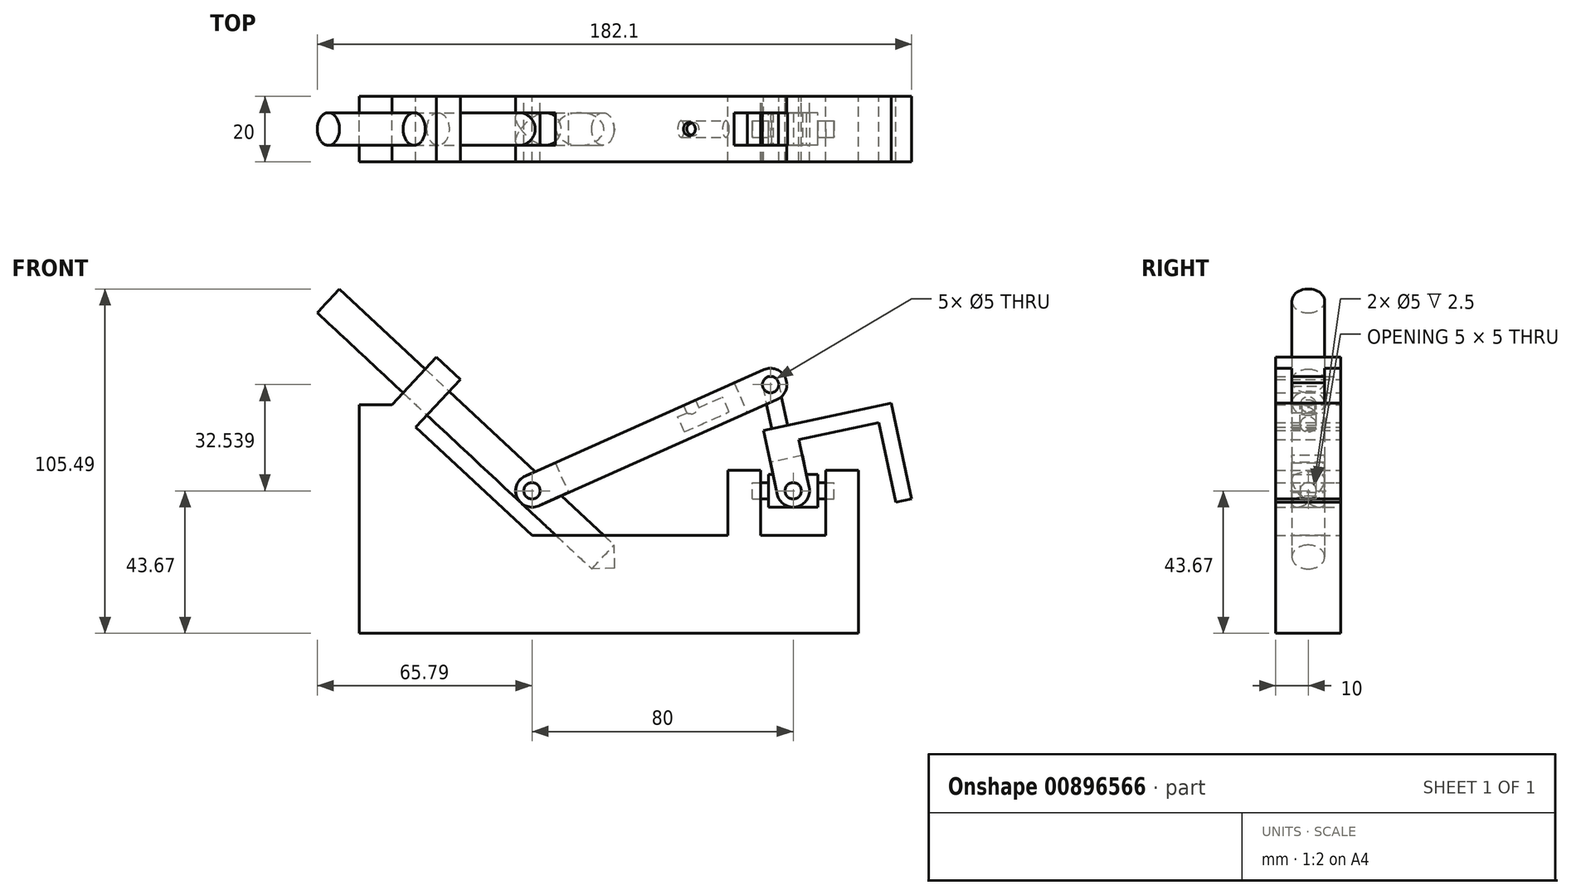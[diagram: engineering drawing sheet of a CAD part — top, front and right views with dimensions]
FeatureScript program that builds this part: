
annotation { "Feature Type Name" : "Feature", "Feature Type Description" : "" }
export const myFeature = defineFeature(function(context is Context, id is Id, definition is map)
    precondition{}
    {
        {
            var Q0;
            Q0=qCreatedBy(makeId("Front.planeOp"),FACE);
            var sketch = newSketch(context, id + "F0", { "sketchPlane" : qUnion([Q0])});
            skLineSegment(sketch, "E0", {"start": v(0, 0) * mm, "end": v(20.8, 0) * mm, "construction": true});
            skLineSegment(sketch, "E1", {"start": v(0, 0) * mm, "end": v(0, 0) * mm});
            skLineSegment(sketch, "E2", {"start": v(0, 0) * mm, "end": v(-25.24, 23.54) * mm, "construction": true});
            skLineSegment(sketch, "E3.MirrorCS", {"start": v(0, 0) * mm, "end": v(20.49, 3.61) * mm, "construction": true});
            skLineSegment(sketch, "E4", {"start": v(0, 0) * mm, "end": v(39.94, 12.21) * mm, "construction": true});
            skLineSegment(sketch, "E5.MirrorCS", {"start": v(0, 0) * mm, "end": v(19, 8.46) * mm, "construction": true});
            skLineSegment(sketch, "E6", {"start": v(19, 8.46) * mm, "end": v(20.49, 3.61) * mm, "construction": true});
            skLineSegment(sketch, "E7", {"start": v(-11.77, -12.62) * mm, "end": v(0, 0) * mm, "construction": true});
            skLineSegment(sketch, "E8", {"start": v(0, 0) * mm, "end": v(2.93, 0) * mm});
            skSolve(sketch);
        }
        {
            var Q0;
            Q0=qCreatedBy(makeId("Front.planeOp"),FACE);
            var sketch = newSketch(context, id + "F1", { "sketchPlane" : qUnion([Q0])});
            skLineSegment(sketch, "E9", {"start": v(0, 0) * mm, "end": v(0, -13.67) * mm, "construction": true});
            skLineSegment(sketch, "E10", {"start": v(0, -13.67) * mm, "end": v(-35.58, 19.5) * mm});
            skLineSegment(sketch, "E11", {"start": v(-42.9, 26.33) * mm, "end": v(-52.9, 26.33) * mm});
            skLineSegment(sketch, "E12", {"start": v(-52.9, 26.33) * mm, "end": v(-52.9, -43.67) * mm});
            skLineSegment(sketch, "E13", {"start": v(-52.9, -43.67) * mm, "end": v(70, -43.67) * mm});
            skLineSegment(sketch, "E14", {"start": v(70, -43.67) * mm, "end": v(70, -13.67) * mm, "construction": true});
            skLineSegment(sketch, "E15", {"start": v(0, -13.67) * mm, "end": v(60, -13.67) * mm});
            skLineSegment(sketch, "E16.0", {"start": v(14.66, -13.67) * mm, "end": v(-56.32, 52.52) * mm, "construction": true});
            skPoint(sketch, "E17.orphan", {"position": v(0, 0) * mm});
            skPoint(sketch, "E18.orphan", {"position": v(-25.24, 23.54) * mm});
            skLineSegment(sketch, "E19", {"start": v(-42.9, 26.33) * mm, "end": v(-29.25, 40.95) * mm});
            skLineSegment(sketch, "E20", {"start": v(-29.25, 40.95) * mm, "end": v(-21.94, 34.13) * mm});
            skLineSegment(sketch, "E21", {"start": v(-21.94, 34.13) * mm, "end": v(-35.58, 19.5) * mm});
            skLineSegment(sketch, "E22", {"start": v(70, -13.67) * mm, "end": v(70, 6.33) * mm});
            skLineSegment(sketch, "E23", {"start": v(70, 6.33) * mm, "end": v(60, 6.33) * mm});
            skLineSegment(sketch, "E24", {"start": v(60, 6.33) * mm, "end": v(60, -13.67) * mm});
            skLineSegment(sketch, "E25", {"start": v(70, -13.67) * mm, "end": v(90, -13.67) * mm});
            skLineSegment(sketch, "E26", {"start": v(90, -13.67) * mm, "end": v(90, 6.33) * mm});
            skLineSegment(sketch, "E27", {"start": v(90, 6.33) * mm, "end": v(100, 6.33) * mm});
            skLineSegment(sketch, "E28", {"start": v(100, 6.33) * mm, "end": v(100, -13.67) * mm});
            skLineSegment(sketch, "E29", {"start": v(100, -13.67) * mm, "end": v(100, -43.67) * mm});
            skLineSegment(sketch, "E30", {"start": v(70, -43.67) * mm, "end": v(100, -43.67) * mm});
            skLineSegment(sketch, "E31", {"start": v(0, -13.67) * mm, "end": v(0, -43.67) * mm, "construction": true});
            skSolve(sketch);
        }
        {
            var Q0;
            Q0=qCreatedBy(makeId("Front.planeOp"),FACE);
            var sketch = newSketch(context, id + "F2", { "sketchPlane" : qUnion([Q0])});
            skLineSegment(sketch, "E32.0", {"start": v(25.39, -23.67) * mm, "end": v(-62.38, 58.17) * mm});
            skPoint(sketch, "E33.orphan", {"position": v(-25.24, 23.54) * mm});
            skLineSegment(sketch, "E34", {"start": v(-62.38, 58.17) * mm, "end": v(-65.79, 54.5) * mm});
            skLineSegment(sketch, "E35", {"start": v(-65.79, 54.5) * mm, "end": v(18.32, -23.92) * mm});
            skPoint(sketch, "E36.orphan", {"position": v(0, 0) * mm});
            skLineSegment(sketch, "E37.0", {"start": v(0, -13.67) * mm, "end": v(60, -13.67) * mm, "construction": true});
            skLineSegment(sketch, "E38", {"start": v(25.39, -23.67) * mm, "end": v(18.32, -23.92) * mm});
            skCircle(sketch, "E39", {"center": v(0, 0) * mm, "radius": 2.5 * mm});
            skSolve(sketch);
        }
        {
            var Q0;
            Q0=qCreatedBy(makeId("Front.planeOp"),FACE);
            var sketch = newSketch(context, id + "F3", { "sketchPlane" : qUnion([Q0])});
            skCircle(sketch, "E40.0", {"center": v(0, 0) * mm, "radius": 2.5 * mm});
            skLineSegment(sketch, "E41.0", {"start": v(0, 0) * mm, "end": v(73.08, 32.54) * mm});
            skLineSegment(sketch, "E42.0", {"start": v(0, 0) * mm, "end": v(80, 0) * mm, "construction": true});
            skLineSegment(sketch, "E43.0", {"start": v(90, -13.67) * mm, "end": v(90, 6.33) * mm});
            skLineSegment(sketch, "E44.0", {"start": v(2.03, -4.57) * mm, "end": v(75.12, 27.97) * mm});
            skLineSegment(sketch, "E45.MirrorCS", {"start": v(-2.03, 4.57) * mm, "end": v(71.05, 37.1) * mm});
            skCircle(sketch, "E46", {"center": v(73.08, 32.54) * mm, "radius": 2.5 * mm});
            skArc(sketch, "E47", {"start": v(-2.03, 4.57) * mm, "mid": v(-4.57, -2.03) * mm, "end": v(2.03, -4.57) * mm});
            skArc(sketch, "E48", {"start": v(71.05, 37.1) * mm, "mid": v(77.65, 34.57) * mm, "end": v(75.12, 27.97) * mm});
            skLineSegment(sketch, "E49", {"start": v(7.1, 8.64) * mm, "end": v(11.17, -0.5) * mm});
            skPoint(sketch, "E50.orphan", {"position": v(9.14, 4.07) * mm});
            skLineSegment(sketch, "E51.0", {"start": v(11.67, 10.67) * mm, "end": v(15.74, 1.53) * mm});
            skLineSegment(sketch, "E52", {"start": v(57.35, 31) * mm, "end": v(61.41, 21.87) * mm});
            skLineSegment(sketch, "E53", {"start": v(58.77, 27.8) * mm, "end": v(47.8, 22.93) * mm});
            skLineSegment(sketch, "E54", {"start": v(45.07, 21.7) * mm, "end": v(46.29, 18.97) * mm});
            skLineSegment(sketch, "E55", {"start": v(49.03, 20.19) * mm, "end": v(60, 25.07) * mm});
            skPoint(sketch, "E56", {"position": v(45.68, 20.34) * mm});
            skLineSegment(sketch, "E57", {"start": v(45.07, 21.7) * mm, "end": v(44.66, 22.62) * mm});
            skLineSegment(sketch, "E58", {"start": v(44.66, 22.62) * mm, "end": v(47.4, 23.84) * mm});
            skLineSegment(sketch, "E59", {"start": v(47.4, 23.84) * mm, "end": v(49.43, 19.27) * mm});
            skLineSegment(sketch, "E60", {"start": v(49.43, 19.27) * mm, "end": v(46.7, 18.05) * mm});
            skLineSegment(sketch, "E61", {"start": v(46.29, 18.97) * mm, "end": v(46.7, 18.05) * mm});
            skLineSegment(sketch, "E62", {"start": v(47.4, 23.84) * mm, "end": v(58.36, 28.72) * mm});
            skLineSegment(sketch, "E63", {"start": v(49.43, 19.27) * mm, "end": v(60.4, 24.15) * mm});
            skLineSegment(sketch, "E64", {"start": v(47.4, 23.84) * mm, "end": v(46.38, 26.12) * mm});
            skLineSegment(sketch, "E65", {"start": v(48.21, 26.94) * mm, "end": v(49.63, 23.74) * mm});
            skLineSegment(sketch, "E66", {"start": v(49.43, 19.27) * mm, "end": v(50.45, 16.99) * mm});
            skLineSegment(sketch, "E67", {"start": v(61.91, 33.04) * mm, "end": v(65.98, 23.9) * mm});
            skSolve(sketch);
        }
        {
            var Q0;
            Q0=qCreatedBy(makeId("Front.planeOp"),FACE);
            var sketch = newSketch(context, id + "F4", { "sketchPlane" : qUnion([Q0])});
            skLineSegment(sketch, "E68.0", {"start": v(0, 0) * mm, "end": v(80, 0) * mm, "construction": true});
            skLineSegment(sketch, "E69.0", {"start": v(70, -13.67) * mm, "end": v(70, 6.33) * mm});
            skLineSegment(sketch, "E70.0", {"start": v(90, -13.67) * mm, "end": v(90, 6.33) * mm});
            skLineSegment(sketch, "E71", {"start": v(80, 0) * mm, "end": v(90, 0) * mm, "construction": true});
            skLineSegment(sketch, "E72.bottom", {"start": v(87.5, 5) * mm, "end": v(72.5, 5) * mm});
            skLineSegment(sketch, "E72.top", {"start": v(87.5, -5) * mm, "end": v(72.5, -5) * mm});
            skLineSegment(sketch, "E72.left", {"start": v(87.5, 5) * mm, "end": v(87.5, 2.5) * mm});
            skLineSegment(sketch, "E72.right", {"start": v(72.5, 5) * mm, "end": v(72.5, 2.5) * mm});
            skPoint(sketch, "E72.middle", {"position": v(80, 0) * mm});
            skCircle(sketch, "E73", {"center": v(80, 0) * mm, "radius": 2.5 * mm});
            skLineSegment(sketch, "E74.bottom", {"start": v(72.5, -2.5) * mm, "end": v(67.5, -2.5) * mm});
            skLineSegment(sketch, "E74.top", {"start": v(72.5, 2.5) * mm, "end": v(67.5, 2.5) * mm});
            skLineSegment(sketch, "E74.right", {"start": v(67.5, -2.5) * mm, "end": v(67.5, 2.5) * mm});
            skPoint(sketch, "E74.middle", {"position": v(70, 0) * mm});
            skLineSegment(sketch, "E75.bottom", {"start": v(87.5, -2.5) * mm, "end": v(92.5, -2.5) * mm});
            skLineSegment(sketch, "E75.top", {"start": v(87.5, 2.5) * mm, "end": v(92.5, 2.5) * mm});
            skLineSegment(sketch, "E75.right", {"start": v(92.5, -2.5) * mm, "end": v(92.5, 2.5) * mm});
            skPoint(sketch, "E75.middle", {"position": v(90, 0) * mm});
            skLineSegment(sketch, "E76.trimOffspring", {"start": v(72.5, -2.5) * mm, "end": v(72.5, -5) * mm});
            skLineSegment(sketch, "E77.trimOffspring", {"start": v(87.5, -2.5) * mm, "end": v(87.5, -5) * mm});
            skLineSegment(sketch, "E78", {"start": v(87.5, -2.5) * mm, "end": v(87.5, 2.5) * mm});
            skLineSegment(sketch, "E79", {"start": v(72.5, -2.5) * mm, "end": v(72.5, 2.5) * mm});
            skLineSegment(sketch, "E80", {"start": v(87.5, 0) * mm, "end": v(92.5, 0) * mm});
            skLineSegment(sketch, "E81", {"start": v(72.5, 0) * mm, "end": v(67.5, 0) * mm});
            skSolve(sketch);
        }
        {
            var Q0;
            Q0=qCreatedBy(makeId("Front.planeOp"),FACE);
            var sketch = newSketch(context, id + "F5", { "sketchPlane" : qUnion([Q0])});
            skCircle(sketch, "E82.0", {"center": v(80, 0) * mm, "radius": 2.5 * mm});
            skArc(sketch, "E83.0", {"start": v(70.64, 32.02) * mm, "mid": v(73.6, 30.1) * mm, "end": v(75.53, 33.06) * mm});
            skLineSegment(sketch, "E84", {"start": v(80, 0) * mm, "end": v(73.08, 32.54) * mm, "construction": true});
            skCircle(sketch, "E85.0", {"center": v(73.08, 32.54) * mm, "radius": 5 * mm, "construction": true});
            skCircle(sketch, "E86.0", {"center": v(80, 0) * mm, "radius": 5 * mm});
            skLineSegment(sketch, "E87", {"start": v(75.1, -1.04) * mm, "end": v(55.36, 91.88) * mm});
            skLineSegment(sketch, "E88.MirrorCS", {"start": v(84.9, 1.04) * mm, "end": v(81.77, 15.71) * mm});
            skPoint(sketch, "E89.orphan", {"position": v(68.2, 31.5) * mm});
            skPoint(sketch, "E90.orphan", {"position": v(77.97, 33.58) * mm});
            skArc(sketch, "E91", {"start": v(55.36, 91.88) * mm, "mid": v(59.2, 97.81) * mm, "end": v(65.14, 93.96) * mm});
            skArc(sketch, "E92", {"start": v(62.7, 93.44) * mm, "mid": v(59.73, 95.37) * mm, "end": v(57.8, 92.4) * mm});
            skLineSegment(sketch, "E93", {"start": v(57.8, 92.4) * mm, "end": v(77.55, -0.52) * mm});
            skLineSegment(sketch, "E94.MirrorCS", {"start": v(62.7, 93.44) * mm, "end": v(82.45, 0.52) * mm});
            skLineSegment(sketch, "E95", {"start": v(80.73, 20.6) * mm, "end": v(110.08, 26.84) * mm});
            skLineSegment(sketch, "E96", {"start": v(110.08, 26.84) * mm, "end": v(116.31, -2.5) * mm});
            skLineSegment(sketch, "E97.0", {"start": v(106.23, 20.9) * mm, "end": v(111.42, -3.54) * mm});
            skLineSegment(sketch, "E97.1", {"start": v(81.77, 15.71) * mm, "end": v(106.23, 20.9) * mm});
            skLineSegment(sketch, "E98", {"start": v(111.42, -3.54) * mm, "end": v(116.31, -2.5) * mm});
            skLineSegment(sketch, "E99.trimOffspring", {"start": v(80.73, 20.6) * mm, "end": v(65.14, 93.96) * mm});
            skLineSegment(sketch, "E100", {"start": v(80.73, 20.6) * mm, "end": v(70.95, 18.52) * mm});
            skLineSegment(sketch, "E101", {"start": v(82.81, 10.82) * mm, "end": v(73.03, 8.74) * mm});
            skSolve(sketch);
        }
        {
            var Q0;
            Q0=makeQuery(id+"F1.imprint","IMPRINT",FACE,{"disambiguationData":[TD([[makeQuery(id+"F1.imprint","IMPRINT",EDGE,{"derivedFrom":sQuery(id+"F1.wireOp",EDGE,"afvjlZ8D-isJQ-Fxy1-4ODG-ZcjdQYL1LsGa")}),-1.0]])]});
            var Q1;
            Q1=makeQuery(id+"F1.imprint","IMPRINT",FACE,{"disambiguationData":[TD([[makeQuery(id+"F1.imprint","IMPRINT",EDGE,{"derivedFrom":sQuery(id+"F1.wireOp",EDGE,"E10")}),1.0]])]});
            extrude(context, id + "F6", {"entities" : qUnion([Q0, Q1]), "endBound" : BoundingType.SYMMETRIC, "depth" : 20 * mm, "offsetDistance" : 25 * mm});
        }
        {
            var Q0;
            Q0=makeQuery(id+"F2.imprint","IMPRINT",FACE,{"disambiguationData":[TD([[makeQuery(id+"F2.imprint","IMPRINT",EDGE,{"derivedFrom":sQuery(id+"F2.wireOp",EDGE,"E32.0")}),1.0]])]});
            var Q1;
            {var subQ0=sQuery(id+"F2.wireOp",EDGE,"E39");var subQ1=sQuery(id+"F2.wireOp",EDGE,"E32.0");var subQ2=makeQuery(id+"F2.imprint","INTERSECT",VERTEX,{"disambiguationData":[OD(0.0)],"derivedFrom":[subQ1,subQ0]});Q1=makeQuery(id+"F2.imprint","IMPRINT",FACE,{"disambiguationData":[TD([[makeQuery(id+"F2.imprint","IMPRINT",EDGE,{"disambiguationData":[TD([[subQ2,-1.0]])],"derivedFrom":subQ1}),1.0]])]});}
            var Q2;
            Q2=sQuery(id+"F2.wireOp",EDGE,"E32.0");
            revolve(context, id + "F7", {"surfaceOperationType" : NewSurfaceOperationType.NEW, "entities" : qUnion([Q0, Q1]), "axis" : qUnion([Q2]), "revolveType" : RevolveType.FULL});
        }
        {
            var Q0;
            {var subQ0=sQuery(id+"F2.wireOp",EDGE,"E39");var subQ1=sQuery(id+"F2.wireOp",EDGE,"E32.0");var subQ2=makeQuery(id+"F2.imprint","INTERSECT",VERTEX,{"disambiguationData":[OD(0.0)],"derivedFrom":[subQ1,subQ0]});Q0=makeQuery(id+"F2.imprint","IMPRINT",FACE,{"disambiguationData":[TD([[makeQuery(id+"F2.imprint","IMPRINT",EDGE,{"disambiguationData":[TD([[subQ2,-1.0]])],"derivedFrom":subQ1}),1.0]])]});}
            var Q1;
            {var subQ0=sQuery(id+"F2.wireOp",EDGE,"E39");var subQ1=sQuery(id+"F2.wireOp",EDGE,"E32.0");var subQ2=makeQuery(id+"F2.imprint","INTERSECT",VERTEX,{"disambiguationData":[OD(0.0)],"derivedFrom":[subQ1,subQ0]});Q1=makeQuery(id+"F2.imprint","IMPRINT",FACE,{"disambiguationData":[TD([[makeQuery(id+"F2.imprint","IMPRINT",EDGE,{"disambiguationData":[TD([[subQ2,-1.0]])],"derivedFrom":subQ1}),-1.0]])]});}
            extrude(context, id + "F8", {"entities" : qUnion([Q0, Q1]), "operationType" : NewBodyOperationType.REMOVE, "endBound" : BoundingType.SYMMETRIC, "oppositeDirection" : true, "depth" : 25 * mm, "offsetDistance" : 25 * mm});
        }
        {
            var Q0;
            Q0=makeQuery(id+"F7.opRevolve","SWEPT_BODY",BODY,{"disambiguationData":[OSD([sQuery(id+"F2.wireOp",EDGE,"E32.0"),sQuery(id+"F2.wireOp",EDGE,"E34"),sQuery(id+"F2.wireOp",EDGE,"E35"),sQuery(id+"F2.wireOp",EDGE,"E38")])]});
            var Q1;
            Q1=makeQuery(id+"F6.opExtrude","SWEPT_BODY",BODY,{"disambiguationData":[OSD([sQuery(id+"F1.wireOp",EDGE,"E10"),sQuery(id+"F1.wireOp",EDGE,"E11"),sQuery(id+"F1.wireOp",EDGE,"E12"),sQuery(id+"F1.wireOp",EDGE,"E13"),sQuery(id+"F1.wireOp",EDGE,"E15"),sQuery(id+"F1.wireOp",EDGE,"E19"),sQuery(id+"F1.wireOp",EDGE,"E20"),sQuery(id+"F1.wireOp",EDGE,"E21"),sQuery(id+"F1.wireOp",EDGE,"E22"),sQuery(id+"F1.wireOp",EDGE,"E23"),sQuery(id+"F1.wireOp",EDGE,"E24"),sQuery(id+"F1.wireOp",EDGE,"E25"),sQuery(id+"F1.wireOp",EDGE,"E26"),sQuery(id+"F1.wireOp",EDGE,"E27"),sQuery(id+"F1.wireOp",EDGE,"E28"),sQuery(id+"F1.wireOp",EDGE,"E29"),sQuery(id+"F1.wireOp",EDGE,"E30")])]});
            booleanBodies(context, id + "F9", {"operationType" : BooleanOperationType.SUBTRACTION, "tools" : qUnion([Q0]), "targets" : qUnion([Q1]), "keepTools" : true});
        }
        {
            var Q0;
            Q0=makeQuery(id+"F3.imprint","IMPRINT",FACE,{"disambiguationData":[TD([[makeQuery(id+"F3.imprint","IMPRINT",EDGE,{"derivedFrom":sQuery(id+"F3.wireOp",EDGE,"E40.0")}),-1.0]])]});
            var Q1;
            {var subQ0=sQuery(id+"F3.wireOp",EDGE,"E49");var subQ1=sQuery(id+"F3.wireOp",EDGE,"E41.0");var subQ2=makeQuery(id+"F3.imprint","INTERSECT",VERTEX,{"derivedFrom":[subQ1,subQ0]});Q1=makeQuery(id+"F3.imprint","IMPRINT",FACE,{"disambiguationData":[TD([[makeQuery(id+"F3.imprint","IMPRINT",EDGE,{"disambiguationData":[TD([[subQ2,-1.0]])],"derivedFrom":subQ1}),1.0]])]});}
            var Q2;
            {var subQ0=sQuery(id+"F3.wireOp",EDGE,"E49");var subQ1=sQuery(id+"F3.wireOp",EDGE,"E41.0");var subQ2=makeQuery(id+"F3.imprint","INTERSECT",VERTEX,{"derivedFrom":[subQ1,subQ0]});Q2=makeQuery(id+"F3.imprint","IMPRINT",FACE,{"disambiguationData":[TD([[makeQuery(id+"F3.imprint","IMPRINT",EDGE,{"disambiguationData":[TD([[subQ2,-1.0]])],"derivedFrom":subQ1}),-1.0]])]});}
            var Q3;
            Q3=makeQuery(id+"F3.imprint","IMPRINT",FACE,{"disambiguationData":[TD([[makeQuery(id+"F3.imprint","IMPRINT",EDGE,{"derivedFrom":sQuery(id+"F3.wireOp",EDGE,"E46")}),-1.0]])]});
            var Q4;
            {var subQ5=sQuery(id+"F3.wireOp",EDGE,"E67");var subQ6=sQuery(id+"F3.wireOp",EDGE,"E41.0");var subQ7=makeQuery(id+"F3.imprint","INTERSECT",VERTEX,{"derivedFrom":[subQ6,subQ5]});Q4=makeQuery(id+"F3.imprint","IMPRINT",FACE,{"disambiguationData":[TD([[makeQuery(id+"F3.imprint","IMPRINT",EDGE,{"disambiguationData":[TD([[subQ7,1.0]])],"derivedFrom":subQ6}),1.0]])]});}
            var Q5;
            {var subQ2=sQuery(id+"F3.wireOp",EDGE,"E41.0");var subQ7=sQuery(id+"F3.wireOp",EDGE,"E67");var subQ9=makeQuery(id+"F3.imprint","INTERSECT",VERTEX,{"derivedFrom":[subQ2,subQ7]});Q5=makeQuery(id+"F3.imprint","IMPRINT",FACE,{"disambiguationData":[TD([[makeQuery(id+"F3.imprint","IMPRINT",EDGE,{"disambiguationData":[TD([[subQ9,1.0]])],"derivedFrom":subQ2}),-1.0]])]});}
            extrude(context, id + "F10", {"entities" : qUnion([Q0, Q1, Q2, Q3, Q4, Q5]), "endBound" : BoundingType.SYMMETRIC, "depth" : 20 * mm, "offsetDistance" : 25 * mm});
        }
        {
            var Q0;
            {var subQ4=sQuery(id+"F3.wireOp",EDGE,"E52");var subQ6=sQuery(id+"F3.wireOp",EDGE,"E41.0");var subQ7=makeQuery(id+"F3.imprint","INTERSECT",VERTEX,{"derivedFrom":[subQ6,subQ4]});Q0=makeQuery(id+"F3.imprint","IMPRINT",FACE,{"disambiguationData":[TD([[makeQuery(id+"F3.imprint","IMPRINT",EDGE,{"disambiguationData":[TD([[subQ7,1.0]])],"derivedFrom":subQ6}),1.0]])]});}
            var Q1;
            {var subQ1=sQuery(id+"F3.wireOp",EDGE,"E57");Q1=makeQuery(id+"F3.imprint","IMPRINT",FACE,{"disambiguationData":[TD([[makeQuery(id+"F3.imprint","IMPRINT",EDGE,{"derivedFrom":subQ1}),-1.0]])]});}
            var Q2;
            Q2=sQuery(id+"F3.wireOp",EDGE,"E41.0");
            revolve(context, id + "F11", {"operationType" : NewBodyOperationType.ADD, "surfaceOperationType" : NewSurfaceOperationType.NEW, "entities" : qUnion([Q0, Q1]), "axis" : qUnion([Q2]), "revolveType" : RevolveType.FULL});
        }
        {
            var Q0;
            {var subQ0=sQuery(id+"F3.wireOp",EDGE,"E57");Q0=makeQuery(id+"F3.imprint","IMPRINT",FACE,{"disambiguationData":[TD([[makeQuery(id+"F3.imprint","IMPRINT",EDGE,{"derivedFrom":subQ0}),1.0]])]});}
            var Q1;
            Q1=makeQuery(id+"F3.imprint","IMPRINT",FACE,{"disambiguationData":[TD([[makeQuery(id+"F3.imprint","IMPRINT",EDGE,{"derivedFrom":sQuery(id+"F3.wireOp",EDGE,"E60")}),1.0]])]});
            var Q2;
            {var subQ0=sQuery(id+"F3.wireOp",EDGE,"E64");Q2=makeQuery(id+"F3.imprint","IMPRINT",FACE,{"disambiguationData":[TD([[makeQuery(id+"F3.imprint","IMPRINT",EDGE,{"derivedFrom":subQ0}),-1.0]])]});}
            var Q3;
            {var subQ0=sQuery(id+"F3.wireOp",EDGE,"E59");var subQ1=sQuery(id+"F3.wireOp",EDGE,"E53");var subQ2=makeQuery(id+"F3.imprint","INTERSECT",VERTEX,{"derivedFrom":[subQ1,subQ0]});Q3=makeQuery(id+"F3.imprint","IMPRINT",FACE,{"disambiguationData":[TD([[makeQuery(id+"F3.imprint","IMPRINT",EDGE,{"disambiguationData":[TD([[subQ2,1.0]])],"derivedFrom":subQ1}),-1.0]])]});}
            var Q4;
            {var subQ0=sQuery(id+"F3.wireOp",EDGE,"E53");var subQ1=sQuery(id+"F3.wireOp",EDGE,"E52");var subQ2=makeQuery(id+"F3.imprint","INTERSECT",VERTEX,{"derivedFrom":[subQ1,subQ0]});Q4=makeQuery(id+"F3.imprint","IMPRINT",FACE,{"disambiguationData":[TD([[makeQuery(id+"F3.imprint","IMPRINT",EDGE,{"disambiguationData":[TD([[subQ2,1.0]])],"derivedFrom":subQ1}),-1.0]])]});}
            var Q5;
            {var subQ0=sQuery(id+"F3.wireOp",EDGE,"E52");var subQ1=sQuery(id+"F3.wireOp",EDGE,"E45.MirrorCS");var subQ2=makeQuery(id+"F3.imprint","INTERSECT",VERTEX,{"derivedFrom":[subQ1,subQ0]});Q5=makeQuery(id+"F3.imprint","IMPRINT",FACE,{"disambiguationData":[TD([[makeQuery(id+"F3.imprint","IMPRINT",EDGE,{"disambiguationData":[TD([[subQ2,1.0]])],"derivedFrom":subQ1}),-1.0]])]});}
            var Q6;
            {var subQ0=sQuery(id+"F3.wireOp",EDGE,"E55");Q6=makeQuery(id+"F3.imprint","IMPRINT",FACE,{"disambiguationData":[TD([[makeQuery(id+"F3.imprint","IMPRINT",EDGE,{"derivedFrom":subQ0}),-1.0]])]});}
            var Q7;
            {var subQ4=sQuery(id+"F3.wireOp",EDGE,"E63");Q7=makeQuery(id+"F3.imprint","IMPRINT",FACE,{"disambiguationData":[TD([[makeQuery(id+"F3.imprint","IMPRINT",EDGE,{"derivedFrom":subQ4}),-1.0]])]});}
            var Q8;
            {var subQ1=sQuery(id+"F3.wireOp",EDGE,"E57");Q8=makeQuery(id+"F3.imprint","IMPRINT",FACE,{"disambiguationData":[TD([[makeQuery(id+"F3.imprint","IMPRINT",EDGE,{"derivedFrom":subQ1}),-1.0]])]});}
            var Q9;
            {var subQ2=sQuery(id+"F3.wireOp",EDGE,"E60");Q9=makeQuery(id+"F3.imprint","IMPRINT",FACE,{"disambiguationData":[TD([[makeQuery(id+"F3.imprint","IMPRINT",EDGE,{"derivedFrom":subQ2}),-1.0]])]});}
            var Q10;
            {var subQ4=sQuery(id+"F3.wireOp",EDGE,"E52");var subQ6=sQuery(id+"F3.wireOp",EDGE,"E41.0");var subQ7=makeQuery(id+"F3.imprint","INTERSECT",VERTEX,{"derivedFrom":[subQ6,subQ4]});Q10=makeQuery(id+"F3.imprint","IMPRINT",FACE,{"disambiguationData":[TD([[makeQuery(id+"F3.imprint","IMPRINT",EDGE,{"disambiguationData":[TD([[subQ7,1.0]])],"derivedFrom":subQ6}),1.0]])]});}
            var Q11;
            {var subQ5=sQuery(id+"F3.wireOp",EDGE,"E55");Q11=makeQuery(id+"F3.imprint","IMPRINT",FACE,{"disambiguationData":[TD([[makeQuery(id+"F3.imprint","IMPRINT",EDGE,{"derivedFrom":subQ5}),1.0]])]});}
            extrude(context, id + "F12", {"entities" : qUnion([Q0, Q1, Q2, Q3, Q4, Q5, Q6, Q7, Q8, Q9, Q10, Q11]), "operationType" : NewBodyOperationType.ADD, "endBound" : BoundingType.SYMMETRIC, "depth" : 20 * mm, "offsetDistance" : 25 * mm});
        }
        {
            var Q0;
            {var subQ1=sQuery(id+"F3.wireOp",EDGE,"E57");Q0=makeQuery(id+"F3.imprint","IMPRINT",FACE,{"disambiguationData":[TD([[makeQuery(id+"F3.imprint","IMPRINT",EDGE,{"derivedFrom":subQ1}),-1.0]])]});}
            var Q1;
            {var subQ4=sQuery(id+"F3.wireOp",EDGE,"E52");var subQ6=sQuery(id+"F3.wireOp",EDGE,"E41.0");var subQ7=makeQuery(id+"F3.imprint","INTERSECT",VERTEX,{"derivedFrom":[subQ6,subQ4]});Q1=makeQuery(id+"F3.imprint","IMPRINT",FACE,{"disambiguationData":[TD([[makeQuery(id+"F3.imprint","IMPRINT",EDGE,{"disambiguationData":[TD([[subQ7,1.0]])],"derivedFrom":subQ6}),1.0]])]});}
            var Q2;
            {var subQ0=sQuery(id+"F3.wireOp",EDGE,"E59");var subQ1=sQuery(id+"F3.wireOp",EDGE,"E53");var subQ2=makeQuery(id+"F3.imprint","INTERSECT",VERTEX,{"derivedFrom":[subQ1,subQ0]});Q2=makeQuery(id+"F3.imprint","IMPRINT",FACE,{"disambiguationData":[TD([[makeQuery(id+"F3.imprint","IMPRINT",EDGE,{"disambiguationData":[TD([[subQ2,1.0]])],"derivedFrom":subQ1}),-1.0]])]});}
            var Q3;
            {var subQ0=sQuery(id+"F3.wireOp",EDGE,"E53");var subQ1=sQuery(id+"F3.wireOp",EDGE,"E52");var subQ2=makeQuery(id+"F3.imprint","INTERSECT",VERTEX,{"derivedFrom":[subQ1,subQ0]});Q3=makeQuery(id+"F3.imprint","IMPRINT",FACE,{"disambiguationData":[TD([[makeQuery(id+"F3.imprint","IMPRINT",EDGE,{"disambiguationData":[TD([[subQ2,1.0]])],"derivedFrom":subQ1}),-1.0]])]});}
            var Q4;
            Q4=sQuery(id+"F3.wireOp",EDGE,"E41.0");
            revolve(context, id + "F13", {"operationType" : NewBodyOperationType.REMOVE, "surfaceOperationType" : NewSurfaceOperationType.NEW, "entities" : qUnion([Q0, Q1, Q2, Q3]), "axis" : qUnion([Q4]), "revolveType" : RevolveType.FULL, "oppositeDirection" : true});
        }
        {
            var Q0;
            {var subQ0=sQuery(id+"F3.wireOp",EDGE,"E64");Q0=makeQuery(id+"F3.imprint","IMPRINT",FACE,{"disambiguationData":[TD([[makeQuery(id+"F3.imprint","IMPRINT",EDGE,{"derivedFrom":subQ0}),-1.0]])]});}
            var Q1;
            {var subQ0=sQuery(id+"F3.wireOp",EDGE,"E59");var subQ1=sQuery(id+"F3.wireOp",EDGE,"E53");var subQ2=makeQuery(id+"F3.imprint","INTERSECT",VERTEX,{"derivedFrom":[subQ1,subQ0]});Q1=makeQuery(id+"F3.imprint","IMPRINT",FACE,{"disambiguationData":[TD([[makeQuery(id+"F3.imprint","IMPRINT",EDGE,{"disambiguationData":[TD([[subQ2,1.0]])],"derivedFrom":subQ1}),-1.0]])]});}
            var Q2;
            Q2=sQuery(id+"F3.wireOp",EDGE,"E65");
            revolve(context, id + "F14", {"operationType" : NewBodyOperationType.REMOVE, "surfaceOperationType" : NewSurfaceOperationType.NEW, "entities" : qUnion([Q0, Q1]), "axis" : qUnion([Q2]), "revolveType" : RevolveType.FULL, "oppositeDirection" : true});
        }
        {
            var Q0;
            Q0=makeQuery(id+"F3.imprint","IMPRINT",FACE,{"disambiguationData":[TD([[makeQuery(id+"F3.imprint","IMPRINT",EDGE,{"derivedFrom":sQuery(id+"F3.wireOp",EDGE,"E40.0")}),-1.0]])]});
            var Q1;
            Q1=makeQuery(id+"F3.imprint","IMPRINT",FACE,{"disambiguationData":[TD([[makeQuery(id+"F3.imprint","IMPRINT",EDGE,{"derivedFrom":sQuery(id+"F3.wireOp",EDGE,"E46")}),-1.0]])]});
            extrude(context, id + "F15", {"entities" : qUnion([Q0, Q1]), "operationType" : NewBodyOperationType.REMOVE, "endBound" : BoundingType.SYMMETRIC, "depth" : 10 * mm, "offsetDistance" : 25 * mm});
        }
        {
            var Q0;
            {var subQ0=sQuery(id+"F4.wireOp",EDGE,"E74.top");var subQ1=sQuery(id+"F4.wireOp",EDGE,"E69.0");var subQ2=makeQuery(id+"F4.imprint","INTERSECT",VERTEX,{"derivedFrom":[subQ1,subQ0]});Q0=makeQuery(id+"F4.imprint","IMPRINT",FACE,{"disambiguationData":[TD([[makeQuery(id+"F4.imprint","IMPRINT",EDGE,{"disambiguationData":[TD([[subQ2,1.0]])],"derivedFrom":subQ1}),-1.0]])]});}
            var Q1;
            {var subQ0=sQuery(id+"F4.wireOp",EDGE,"E75.top");var subQ1=sQuery(id+"F4.wireOp",EDGE,"E70.0");var subQ2=makeQuery(id+"F4.imprint","INTERSECT",VERTEX,{"derivedFrom":[subQ1,subQ0]});Q1=makeQuery(id+"F4.imprint","IMPRINT",FACE,{"disambiguationData":[TD([[makeQuery(id+"F4.imprint","IMPRINT",EDGE,{"disambiguationData":[TD([[subQ2,1.0]])],"derivedFrom":subQ1}),1.0]])]});}
            var Q2;
            {var subQ0=sQuery(id+"F4.wireOp",EDGE,"E74.top");var subQ1=sQuery(id+"F4.wireOp",EDGE,"E69.0");var subQ2=makeQuery(id+"F4.imprint","INTERSECT",VERTEX,{"derivedFrom":[subQ1,subQ0]});Q2=makeQuery(id+"F4.imprint","IMPRINT",FACE,{"disambiguationData":[TD([[makeQuery(id+"F4.imprint","IMPRINT",EDGE,{"disambiguationData":[TD([[subQ2,1.0]])],"derivedFrom":subQ1}),1.0]])]});}
            var Q3;
            {var subQ0=sQuery(id+"F4.wireOp",EDGE,"E75.top");var subQ1=sQuery(id+"F4.wireOp",EDGE,"E70.0");var subQ2=makeQuery(id+"F4.imprint","INTERSECT",VERTEX,{"derivedFrom":[subQ1,subQ0]});Q3=makeQuery(id+"F4.imprint","IMPRINT",FACE,{"disambiguationData":[TD([[makeQuery(id+"F4.imprint","IMPRINT",EDGE,{"disambiguationData":[TD([[subQ2,1.0]])],"derivedFrom":subQ1}),-1.0]])]});}
            var Q4;
            Q4=sQuery(id+"F4.wireOp",EDGE,"E81");
            revolve(context, id + "F16", {"surfaceOperationType" : NewSurfaceOperationType.NEW, "entities" : qUnion([Q0, Q1, Q2, Q3]), "axis" : qUnion([Q4]), "revolveType" : RevolveType.FULL});
        }
        {
            var Q0;
            Q0=makeQuery(id+"F4.imprint","IMPRINT",FACE,{"disambiguationData":[TD([[makeQuery(id+"F4.imprint","IMPRINT",EDGE,{"derivedFrom":sQuery(id+"F4.wireOp",EDGE,"E72.bottom")}),1.0]])]});
            extrude(context, id + "F17", {"entities" : qUnion([Q0]), "operationType" : NewBodyOperationType.ADD, "endBound" : BoundingType.SYMMETRIC, "depth" : 10 * mm, "offsetDistance" : 25 * mm});
        }
        {
            var Q0;
            Q0=makeQuery(id+"F16.opRevolve","SWEPT_BODY",BODY,{"disambiguationData":[OSD([sQuery(id+"F4.wireOp",EDGE,"E74.top"),sQuery(id+"F4.wireOp",EDGE,"E74.right"),sQuery(id+"F4.wireOp",EDGE,"E79"),sQuery(id+"F4.wireOp",EDGE,"E81")])]});
            var Q1;
            Q1=makeQuery(id+"F6.opExtrude","SWEPT_BODY",BODY,{"disambiguationData":[OSD([sQuery(id+"F1.wireOp",EDGE,"E10"),sQuery(id+"F1.wireOp",EDGE,"E11"),sQuery(id+"F1.wireOp",EDGE,"E12"),sQuery(id+"F1.wireOp",EDGE,"E13"),sQuery(id+"F1.wireOp",EDGE,"E15"),sQuery(id+"F1.wireOp",EDGE,"E19"),sQuery(id+"F1.wireOp",EDGE,"E20"),sQuery(id+"F1.wireOp",EDGE,"E21"),sQuery(id+"F1.wireOp",EDGE,"E22"),sQuery(id+"F1.wireOp",EDGE,"E23"),sQuery(id+"F1.wireOp",EDGE,"E24"),sQuery(id+"F1.wireOp",EDGE,"E25"),sQuery(id+"F1.wireOp",EDGE,"E26"),sQuery(id+"F1.wireOp",EDGE,"E27"),sQuery(id+"F1.wireOp",EDGE,"E28"),sQuery(id+"F1.wireOp",EDGE,"E29"),sQuery(id+"F1.wireOp",EDGE,"E30")])]});
            booleanBodies(context, id + "F18", {"operationType" : BooleanOperationType.SUBTRACTION, "tools" : qUnion([Q0]), "targets" : qUnion([Q1]), "keepTools" : true});
        }
        {
            var Q0;
            {var subQ0=sQuery(id+"F5.wireOp",EDGE,"E88.MirrorCS");var subQ1=sQuery(id+"F5.wireOp",EDGE,"E86.0");var subQ2=makeQuery(id+"F5.imprint","INTERSECT",VERTEX,{"derivedFrom":[subQ1,subQ0]});Q0=makeQuery(id+"F5.imprint","IMPRINT",FACE,{"disambiguationData":[TD([[makeQuery(id+"F5.imprint","IMPRINT",EDGE,{"disambiguationData":[TD([[subQ2,-1.0]])],"derivedFrom":subQ1}),-1.0]])]});}
            var Q1;
            {var subQ0=sQuery(id+"F5.wireOp",EDGE,"E94.MirrorCS");var subQ1=sQuery(id+"F5.wireOp",EDGE,"E86.0");var subQ2=makeQuery(id+"F5.imprint","INTERSECT",VERTEX,{"derivedFrom":[subQ1,subQ0]});Q1=makeQuery(id+"F5.imprint","IMPRINT",FACE,{"disambiguationData":[TD([[makeQuery(id+"F5.imprint","IMPRINT",EDGE,{"disambiguationData":[TD([[subQ2,-1.0]])],"derivedFrom":subQ1}),-1.0]])]});}
            var Q2;
            {var subQ0=sQuery(id+"F5.wireOp",EDGE,"E87");var subQ1=sQuery(id+"F5.wireOp",EDGE,"E86.0");var subQ2=makeQuery(id+"F5.imprint","INTERSECT",VERTEX,{"derivedFrom":[subQ1,subQ0]});Q2=makeQuery(id+"F5.imprint","IMPRINT",FACE,{"disambiguationData":[TD([[makeQuery(id+"F5.imprint","IMPRINT",EDGE,{"disambiguationData":[TD([[subQ2,1.0]])],"derivedFrom":subQ1}),-1.0]])]});}
            var Q3;
            {var subQ2=sQuery(id+"F5.wireOp",EDGE,"E93");var subQ7=sQuery(id+"F5.wireOp",EDGE,"E82.0");var subQ8=makeQuery(id+"F5.imprint","INTERSECT",VERTEX,{"derivedFrom":[subQ7,subQ2]});Q3=makeQuery(id+"F5.imprint","IMPRINT",FACE,{"disambiguationData":[TD([[makeQuery(id+"F5.imprint","IMPRINT",EDGE,{"disambiguationData":[TD([[subQ8,-1.0]])],"derivedFrom":subQ7}),-1.0]])]});}
            var Q4;
            {var subQ0=sQuery(id+"F5.wireOp",EDGE,"E93");var subQ1=sQuery(id+"F5.wireOp",EDGE,"E82.0");var subQ2=makeQuery(id+"F5.imprint","INTERSECT",VERTEX,{"derivedFrom":[subQ1,subQ0]});Q4=makeQuery(id+"F5.imprint","IMPRINT",FACE,{"disambiguationData":[TD([[makeQuery(id+"F5.imprint","IMPRINT",EDGE,{"disambiguationData":[TD([[subQ2,1.0]])],"derivedFrom":subQ1}),-1.0]])]});}
            var Q5;
            {var subQ0=sQuery(id+"F5.wireOp",EDGE,"E100");var subQ1=sQuery(id+"F5.wireOp",EDGE,"E93");var subQ2=makeQuery(id+"F5.imprint","INTERSECT",VERTEX,{"derivedFrom":[subQ1,subQ0]});Q5=makeQuery(id+"F5.imprint","IMPRINT",FACE,{"disambiguationData":[TD([[makeQuery(id+"F5.imprint","IMPRINT",EDGE,{"disambiguationData":[TD([[subQ2,-1.0]])],"derivedFrom":subQ1}),1.0]])]});}
            var Q6;
            {var subQ0=sQuery(id+"F5.wireOp",EDGE,"E100");var subQ1=sQuery(id+"F5.wireOp",EDGE,"E87");var subQ2=makeQuery(id+"F5.imprint","INTERSECT",VERTEX,{"derivedFrom":[subQ1,subQ0]});Q6=makeQuery(id+"F5.imprint","IMPRINT",FACE,{"disambiguationData":[TD([[makeQuery(id+"F5.imprint","IMPRINT",EDGE,{"disambiguationData":[TD([[subQ2,1.0]])],"derivedFrom":subQ1}),-1.0]])]});}
            var Q7;
            {var subQ0=sQuery(id+"F5.wireOp",EDGE,"E95");Q7=makeQuery(id+"F5.imprint","IMPRINT",FACE,{"disambiguationData":[TD([[makeQuery(id+"F5.imprint","IMPRINT",EDGE,{"derivedFrom":subQ0}),-1.0]])]});}
            extrude(context, id + "F19", {"entities" : qUnion([Q0, Q1, Q2, Q3, Q4, Q5, Q6, Q7]), "endBound" : BoundingType.SYMMETRIC, "depth" : 20 * mm, "offsetDistance" : 25 * mm});
        }
        {
            var Q0;
            {var subQ1=sQuery(id+"F5.wireOp",EDGE,"E91");Q0=makeQuery(id+"F5.imprint","IMPRINT",FACE,{"disambiguationData":[TD([[makeQuery(id+"F5.imprint","IMPRINT",EDGE,{"derivedFrom":subQ1}),-1.0]])]});}
            var Q1;
            {var subQ0=sQuery(id+"F5.wireOp",EDGE,"E83.0");Q1=makeQuery(id+"F5.imprint","IMPRINT",FACE,{"disambiguationData":[TD([[makeQuery(id+"F5.imprint","IMPRINT",EDGE,{"derivedFrom":subQ0}),-1.0]])]});}
            extrude(context, id + "F20", {"entities" : qUnion([Q0, Q1]), "operationType" : NewBodyOperationType.ADD, "endBound" : BoundingType.SYMMETRIC, "depth" : 10 * mm, "offsetDistance" : 25 * mm});
        }
        {
            var Q0;
            {var subQ0=sQuery(id+"F5.wireOp",EDGE,"E94.MirrorCS");var subQ1=sQuery(id+"F5.wireOp",EDGE,"E86.0");var subQ2=makeQuery(id+"F5.imprint","INTERSECT",VERTEX,{"derivedFrom":[subQ1,subQ0]});Q0=makeQuery(id+"F5.imprint","IMPRINT",FACE,{"disambiguationData":[TD([[makeQuery(id+"F5.imprint","IMPRINT",EDGE,{"disambiguationData":[TD([[subQ2,-1.0]])],"derivedFrom":subQ1}),-1.0]])]});}
            var Q1;
            {var subQ0=sQuery(id+"F5.wireOp",EDGE,"E88.MirrorCS");var subQ1=sQuery(id+"F5.wireOp",EDGE,"E86.0");var subQ2=makeQuery(id+"F5.imprint","INTERSECT",VERTEX,{"derivedFrom":[subQ1,subQ0]});Q1=makeQuery(id+"F5.imprint","IMPRINT",FACE,{"disambiguationData":[TD([[makeQuery(id+"F5.imprint","IMPRINT",EDGE,{"disambiguationData":[TD([[subQ2,-1.0]])],"derivedFrom":subQ1}),-1.0]])]});}
            var Q2;
            {var subQ0=sQuery(id+"F5.wireOp",EDGE,"E87");var subQ1=sQuery(id+"F5.wireOp",EDGE,"E86.0");var subQ2=makeQuery(id+"F5.imprint","INTERSECT",VERTEX,{"derivedFrom":[subQ1,subQ0]});Q2=makeQuery(id+"F5.imprint","IMPRINT",FACE,{"disambiguationData":[TD([[makeQuery(id+"F5.imprint","IMPRINT",EDGE,{"disambiguationData":[TD([[subQ2,1.0]])],"derivedFrom":subQ1}),-1.0]])]});}
            var Q3;
            {var subQ2=sQuery(id+"F5.wireOp",EDGE,"E93");var subQ7=sQuery(id+"F5.wireOp",EDGE,"E82.0");var subQ8=makeQuery(id+"F5.imprint","INTERSECT",VERTEX,{"derivedFrom":[subQ7,subQ2]});Q3=makeQuery(id+"F5.imprint","IMPRINT",FACE,{"disambiguationData":[TD([[makeQuery(id+"F5.imprint","IMPRINT",EDGE,{"disambiguationData":[TD([[subQ8,-1.0]])],"derivedFrom":subQ7}),-1.0]])]});}
            var Q4;
            {var subQ0=sQuery(id+"F5.wireOp",EDGE,"E93");var subQ1=sQuery(id+"F5.wireOp",EDGE,"E82.0");var subQ2=makeQuery(id+"F5.imprint","INTERSECT",VERTEX,{"derivedFrom":[subQ1,subQ0]});Q4=makeQuery(id+"F5.imprint","IMPRINT",FACE,{"disambiguationData":[TD([[makeQuery(id+"F5.imprint","IMPRINT",EDGE,{"disambiguationData":[TD([[subQ2,1.0]])],"derivedFrom":subQ1}),-1.0]])]});}
            extrude(context, id + "F21", {"entities" : qUnion([Q0, Q1, Q2, Q3, Q4]), "operationType" : NewBodyOperationType.REMOVE, "endBound" : BoundingType.SYMMETRIC, "oppositeDirection" : true, "depth" : 10 * mm, "offsetDistance" : 25 * mm});
        }
        {
            var Q0;
            {var subQ0=sQuery(id+"F2.wireOp",EDGE,"E39");var subQ1=sQuery(id+"F2.wireOp",EDGE,"E32.0");var subQ2=makeQuery(id+"F2.imprint","INTERSECT",VERTEX,{"disambiguationData":[OD(0.0)],"derivedFrom":[subQ1,subQ0]});Q0=makeQuery(id+"F2.imprint","IMPRINT",FACE,{"disambiguationData":[TD([[makeQuery(id+"F2.imprint","IMPRINT",EDGE,{"disambiguationData":[TD([[subQ2,-1.0]])],"derivedFrom":subQ1}),1.0]])]});}
            var Q1;
            {var subQ0=sQuery(id+"F2.wireOp",EDGE,"E39");var subQ1=sQuery(id+"F2.wireOp",EDGE,"E32.0");var subQ2=makeQuery(id+"F2.imprint","INTERSECT",VERTEX,{"disambiguationData":[OD(0.0)],"derivedFrom":[subQ1,subQ0]});Q1=makeQuery(id+"F2.imprint","IMPRINT",FACE,{"disambiguationData":[TD([[makeQuery(id+"F2.imprint","IMPRINT",EDGE,{"disambiguationData":[TD([[subQ2,-1.0]])],"derivedFrom":subQ1}),-1.0]])]});}
            var Q2;
            {var subQ0=sQuery(id+"F5.wireOp",EDGE,"E82.0");var subQ1=makeQuery(id+"F5.imprint","INTERSECT",VERTEX,{"derivedFrom":[subQ0,sQuery(id+"F5.wireOp",EDGE,"E93")]});Q2=makeQuery(id+"F5.imprint","IMPRINT",FACE,{"disambiguationData":[TD([[makeQuery(id+"F5.imprint","IMPRINT",EDGE,{"disambiguationData":[TD([[subQ1,1.0]])],"derivedFrom":subQ0}),1.0]])]});}
            var Q3;
            Q3=makeQuery(id+"F3.imprint","IMPRINT",FACE,{"disambiguationData":[TD([[makeQuery(id+"F3.imprint","IMPRINT",EDGE,{"derivedFrom":sQuery(id+"F3.wireOp",EDGE,"E46")}),1.0]])]});
            extrude(context, id + "F22", {"entities" : qUnion([Q0, Q1, Q2, Q3]), "endBound" : BoundingType.SYMMETRIC, "depth" : 20 * mm, "offsetDistance" : 25 * mm});
        }
    });
